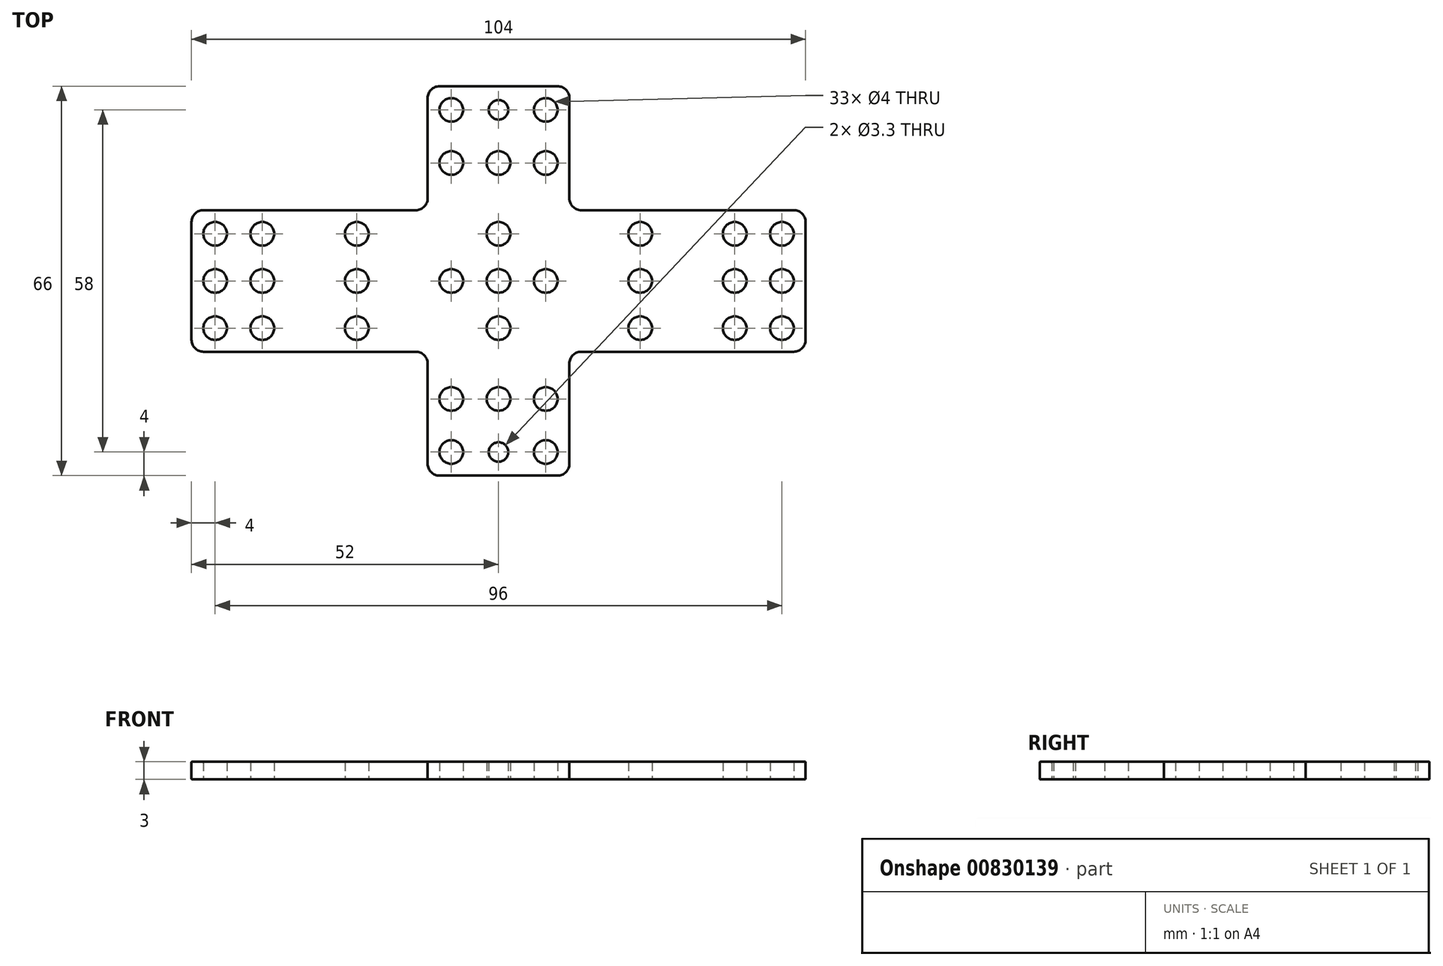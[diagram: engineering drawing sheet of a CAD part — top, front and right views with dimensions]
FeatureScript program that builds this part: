
annotation { "Feature Type Name" : "Feature", "Feature Type Description" : "" }
export const myFeature = defineFeature(function(context is Context, id is Id, definition is map)
    precondition{}
    {
        {
            var Q0;
            Q0=qCreatedBy(makeId("Top.planeOp"),FACE);
            var sketch = newSketch(context, id + "F0", { "sketchPlane" : qUnion([Q0])});
            skLineSegment(sketch, "E0", {"start": v(-10, -33) * mm, "end": v(10, -33) * mm});
            skLineSegment(sketch, "E1", {"start": v(52, -10) * mm, "end": v(52, 10) * mm});
            skLineSegment(sketch, "E2", {"start": v(10, 33) * mm, "end": v(-10, 33) * mm});
            skLineSegment(sketch, "E3", {"start": v(-52, 10) * mm, "end": v(-52, -10) * mm});
            skLineSegment(sketch, "E4", {"start": v(-50, 12) * mm, "end": v(-14, 12) * mm});
            skLineSegment(sketch, "E5", {"start": v(-12, 14) * mm, "end": v(-12, 31) * mm});
            skLineSegment(sketch, "E6", {"start": v(-50, -12) * mm, "end": v(-14, -12) * mm});
            skLineSegment(sketch, "E7", {"start": v(-12, -14) * mm, "end": v(-12, -31) * mm});
            skLineSegment(sketch, "E8", {"start": v(12, 31) * mm, "end": v(12, 14) * mm});
            skLineSegment(sketch, "E9", {"start": v(14, 12) * mm, "end": v(50, 12) * mm});
            skLineSegment(sketch, "E10", {"start": v(50, -12) * mm, "end": v(14, -12) * mm});
            skLineSegment(sketch, "E11", {"start": v(12, -14) * mm, "end": v(12, -31) * mm});
            skPoint(sketch, "E12.visualSharp", {"position": v(-52, 12) * mm});
            skArc(sketch, "E12.filletArc", {"start": v(-50, 12) * mm, "mid": v(-51.41, 11.41) * mm, "end": v(-52, 10) * mm});
            skPoint(sketch, "E13.visualSharp", {"position": v(-12, 12) * mm});
            skArc(sketch, "E13.filletArc", {"start": v(-14, 12) * mm, "mid": v(-12.59, 12.59) * mm, "end": v(-12, 14) * mm});
            skPoint(sketch, "E14.visualSharp", {"position": v(-12, 33) * mm});
            skArc(sketch, "E14.filletArc", {"start": v(-10, 33) * mm, "mid": v(-11.41, 32.41) * mm, "end": v(-12, 31) * mm});
            skPoint(sketch, "E15.visualSharp", {"position": v(12, 33) * mm});
            skArc(sketch, "E15.filletArc", {"start": v(12, 31) * mm, "mid": v(11.41, 32.41) * mm, "end": v(10, 33) * mm});
            skPoint(sketch, "E16.visualSharp", {"position": v(12, 12) * mm});
            skArc(sketch, "E16.filletArc", {"start": v(12, 14) * mm, "mid": v(12.59, 12.59) * mm, "end": v(14, 12) * mm});
            skPoint(sketch, "E17.visualSharp", {"position": v(52, 12) * mm});
            skArc(sketch, "E17.filletArc", {"start": v(52, 10) * mm, "mid": v(51.41, 11.41) * mm, "end": v(50, 12) * mm});
            skPoint(sketch, "E18.visualSharp", {"position": v(52, -12) * mm});
            skArc(sketch, "E18.filletArc", {"start": v(50, -12) * mm, "mid": v(51.41, -11.41) * mm, "end": v(52, -10) * mm});
            skPoint(sketch, "E19.visualSharp", {"position": v(12, -12) * mm});
            skArc(sketch, "E19.filletArc", {"start": v(14, -12) * mm, "mid": v(12.59, -12.59) * mm, "end": v(12, -14) * mm});
            skPoint(sketch, "E20.visualSharp", {"position": v(12, -33) * mm});
            skArc(sketch, "E20.filletArc", {"start": v(10, -33) * mm, "mid": v(11.41, -32.41) * mm, "end": v(12, -31) * mm});
            skPoint(sketch, "E21.visualSharp", {"position": v(-12, -33) * mm});
            skArc(sketch, "E21.filletArc", {"start": v(-12, -31) * mm, "mid": v(-11.41, -32.41) * mm, "end": v(-10, -33) * mm});
            skPoint(sketch, "E22.visualSharp", {"position": v(-12, -12) * mm});
            skArc(sketch, "E22.filletArc", {"start": v(-12, -14) * mm, "mid": v(-12.59, -12.59) * mm, "end": v(-14, -12) * mm});
            skPoint(sketch, "E23.visualSharp", {"position": v(-52, -12) * mm});
            skArc(sketch, "E23.filletArc", {"start": v(-52, -10) * mm, "mid": v(-51.41, -11.41) * mm, "end": v(-50, -12) * mm});
            skPoint(sketch, "E24", {"position": v(0, 0) * mm});
            skPoint(sketch, "E25", {"position": v(8, 0) * mm});
            skPoint(sketch, "E26", {"position": v(0, -8) * mm});
            skPoint(sketch, "E27", {"position": v(-8, 0) * mm});
            skPoint(sketch, "E28", {"position": v(0, 8) * mm});
            skCircle(sketch, "E29", {"center": v(0, 0) * mm, "radius": 2 * mm});
            skCircle(sketch, "E30", {"center": v(8, 0) * mm, "radius": 2 * mm});
            skCircle(sketch, "E31", {"center": v(-8, 0) * mm, "radius": 2 * mm});
            skCircle(sketch, "E32", {"center": v(0, -8) * mm, "radius": 2 * mm});
            skCircle(sketch, "E33", {"center": v(0, 8) * mm, "radius": 2 * mm});
            skCircle(sketch, "E34", {"center": v(24, 0) * mm, "radius": 2 * mm});
            skCircle(sketch, "E35", {"center": v(24, 8) * mm, "radius": 2 * mm});
            skCircle(sketch, "E36", {"center": v(24, -8) * mm, "radius": 2 * mm});
            skCircle(sketch, "E37", {"center": v(40, 0) * mm, "radius": 2 * mm});
            skCircle(sketch, "E38", {"center": v(40, 8) * mm, "radius": 2 * mm});
            skCircle(sketch, "E39", {"center": v(40, -8) * mm, "radius": 2 * mm});
            skCircle(sketch, "E40", {"center": v(48, 0) * mm, "radius": 2 * mm});
            skCircle(sketch, "E41", {"center": v(48, -8) * mm, "radius": 2 * mm});
            skCircle(sketch, "E42", {"center": v(48, 8) * mm, "radius": 2 * mm});
            skCircle(sketch, "E43.MirrorC", {"center": v(-24, -8) * mm, "radius": 2 * mm});
            skCircle(sketch, "E44.MirrorC", {"center": v(-48, 0) * mm, "radius": 2 * mm});
            skCircle(sketch, "E45.MirrorC", {"center": v(-40, 0) * mm, "radius": 2 * mm});
            skCircle(sketch, "E46.MirrorC", {"center": v(-40, 8) * mm, "radius": 2 * mm});
            skCircle(sketch, "E47.MirrorC", {"center": v(-24, 0) * mm, "radius": 2 * mm});
            skCircle(sketch, "E48.MirrorC", {"center": v(-48, 8) * mm, "radius": 2 * mm});
            skCircle(sketch, "E49.MirrorC", {"center": v(-48, -8) * mm, "radius": 2 * mm});
            skCircle(sketch, "E50.MirrorC", {"center": v(-24, 8) * mm, "radius": 2 * mm});
            skCircle(sketch, "E51.MirrorC", {"center": v(-40, -8) * mm, "radius": 2 * mm});
            skCircle(sketch, "E52", {"center": v(0, 20) * mm, "radius": 2 * mm});
            skCircle(sketch, "E53", {"center": v(8, 20) * mm, "radius": 2 * mm});
            skCircle(sketch, "E54", {"center": v(-8, 20) * mm, "radius": 2 * mm});
            skCircle(sketch, "E55.MirrorC", {"center": v(-8, -20) * mm, "radius": 2 * mm});
            skCircle(sketch, "E56.MirrorC", {"center": v(0, -20) * mm, "radius": 2 * mm});
            skCircle(sketch, "E57.MirrorC", {"center": v(8, -20) * mm, "radius": 2 * mm});
            skCircle(sketch, "E58", {"center": v(8, 29) * mm, "radius": 2 * mm});
            skCircle(sketch, "E59", {"center": v(-8, 29) * mm, "radius": 2 * mm});
            skPoint(sketch, "E60", {"position": v(0, 29) * mm});
            skPoint(sketch, "E61.MirrorP", {"position": v(0, -29) * mm});
            skCircle(sketch, "E62.MirrorC", {"center": v(-8, -29) * mm, "radius": 2 * mm});
            skCircle(sketch, "E63.MirrorC", {"center": v(8, -29) * mm, "radius": 2 * mm});
            skSolve(sketch);
        }
        {
            var Q0;
            Q0 = qSketchRegion(id + "F0", true);
            extrude(context, id + "F1", {"entities" : qUnion([Q0]), "depth" : 3 * mm, "offsetDistance" : 25 * mm});
        }
        {
            var Q0;
            Q0=makeQuery(id+"F1.opExtrude","CAP_FACE",FACE,{"disambiguationData":[OSD([sQuery(id+"F0.wireOp",EDGE,"E0"),sQuery(id+"F0.wireOp",EDGE,"E1"),sQuery(id+"F0.wireOp",EDGE,"E2"),sQuery(id+"F0.wireOp",EDGE,"E3"),sQuery(id+"F0.wireOp",EDGE,"E4"),sQuery(id+"F0.wireOp",EDGE,"E5"),sQuery(id+"F0.wireOp",EDGE,"E6"),sQuery(id+"F0.wireOp",EDGE,"E7"),sQuery(id+"F0.wireOp",EDGE,"E8"),sQuery(id+"F0.wireOp",EDGE,"E9"),sQuery(id+"F0.wireOp",EDGE,"E10"),sQuery(id+"F0.wireOp",EDGE,"E11"),sQuery(id+"F0.wireOp",EDGE,"E12.filletArc"),sQuery(id+"F0.wireOp",EDGE,"E13.filletArc"),sQuery(id+"F0.wireOp",EDGE,"E14.filletArc"),sQuery(id+"F0.wireOp",EDGE,"E15.filletArc"),sQuery(id+"F0.wireOp",EDGE,"E16.filletArc"),sQuery(id+"F0.wireOp",EDGE,"E17.filletArc"),sQuery(id+"F0.wireOp",EDGE,"E18.filletArc"),sQuery(id+"F0.wireOp",EDGE,"E19.filletArc"),sQuery(id+"F0.wireOp",EDGE,"E20.filletArc"),sQuery(id+"F0.wireOp",EDGE,"E21.filletArc"),sQuery(id+"F0.wireOp",EDGE,"E22.filletArc"),sQuery(id+"F0.wireOp",EDGE,"E23.filletArc"),sQuery(id+"F0.wireOp",EDGE,"E29"),sQuery(id+"F0.wireOp",EDGE,"E30"),sQuery(id+"F0.wireOp",EDGE,"E31"),sQuery(id+"F0.wireOp",EDGE,"E32"),sQuery(id+"F0.wireOp",EDGE,"E33"),sQuery(id+"F0.wireOp",EDGE,"E34"),sQuery(id+"F0.wireOp",EDGE,"E35"),sQuery(id+"F0.wireOp",EDGE,"E36"),sQuery(id+"F0.wireOp",EDGE,"E37"),sQuery(id+"F0.wireOp",EDGE,"E38"),sQuery(id+"F0.wireOp",EDGE,"E39"),sQuery(id+"F0.wireOp",EDGE,"E40"),sQuery(id+"F0.wireOp",EDGE,"E41"),sQuery(id+"F0.wireOp",EDGE,"E42"),sQuery(id+"F0.wireOp",EDGE,"E43.MirrorC"),sQuery(id+"F0.wireOp",EDGE,"E44.MirrorC"),sQuery(id+"F0.wireOp",EDGE,"E45.MirrorC"),sQuery(id+"F0.wireOp",EDGE,"E46.MirrorC"),sQuery(id+"F0.wireOp",EDGE,"E47.MirrorC"),sQuery(id+"F0.wireOp",EDGE,"E48.MirrorC"),sQuery(id+"F0.wireOp",EDGE,"E49.MirrorC"),sQuery(id+"F0.wireOp",EDGE,"E50.MirrorC"),sQuery(id+"F0.wireOp",EDGE,"E51.MirrorC"),sQuery(id+"F0.wireOp",EDGE,"E52"),sQuery(id+"F0.wireOp",EDGE,"E53"),sQuery(id+"F0.wireOp",EDGE,"E54"),sQuery(id+"F0.wireOp",EDGE,"E58"),sQuery(id+"F0.wireOp",EDGE,"E59"),sQuery(id+"F0.wireOp",EDGE,"E56.MirrorC"),sQuery(id+"F0.wireOp",EDGE,"E55.MirrorC"),sQuery(id+"F0.wireOp",EDGE,"E62.MirrorC"),sQuery(id+"F0.wireOp",EDGE,"E63.MirrorC"),sQuery(id+"F0.wireOp",EDGE,"E57.MirrorC")])],"isStart":true});
            var sketch = newSketch(context, id + "F2", { "sketchPlane" : qUnion([Q0])});
            skPoint(sketch, "E64", {"position": v(0, 29) * mm});
            skPoint(sketch, "E65", {"position": v(0, -29) * mm});
            skSolve(sketch);
        }
        {
            var Q0;
            Q0=sQuery(id+"F2.wireOp",VERTEX,"E64");
            var Q1;
            Q1=sQuery(id+"F2.wireOp",VERTEX,"E65");
            var Q2;
            Q2=makeQuery(id+"F1.opExtrude","SWEPT_BODY",BODY,{"disambiguationData":[OSD([sQuery(id+"F0.wireOp",EDGE,"E0"),sQuery(id+"F0.wireOp",EDGE,"E1"),sQuery(id+"F0.wireOp",EDGE,"E2"),sQuery(id+"F0.wireOp",EDGE,"E3"),sQuery(id+"F0.wireOp",EDGE,"E4"),sQuery(id+"F0.wireOp",EDGE,"E5"),sQuery(id+"F0.wireOp",EDGE,"E6"),sQuery(id+"F0.wireOp",EDGE,"E7"),sQuery(id+"F0.wireOp",EDGE,"E8"),sQuery(id+"F0.wireOp",EDGE,"E9"),sQuery(id+"F0.wireOp",EDGE,"E10"),sQuery(id+"F0.wireOp",EDGE,"E11"),sQuery(id+"F0.wireOp",EDGE,"E12.filletArc"),sQuery(id+"F0.wireOp",EDGE,"E13.filletArc"),sQuery(id+"F0.wireOp",EDGE,"E14.filletArc"),sQuery(id+"F0.wireOp",EDGE,"E15.filletArc"),sQuery(id+"F0.wireOp",EDGE,"E16.filletArc"),sQuery(id+"F0.wireOp",EDGE,"E17.filletArc"),sQuery(id+"F0.wireOp",EDGE,"E18.filletArc"),sQuery(id+"F0.wireOp",EDGE,"E19.filletArc"),sQuery(id+"F0.wireOp",EDGE,"E20.filletArc"),sQuery(id+"F0.wireOp",EDGE,"E21.filletArc"),sQuery(id+"F0.wireOp",EDGE,"E22.filletArc"),sQuery(id+"F0.wireOp",EDGE,"E23.filletArc"),sQuery(id+"F0.wireOp",EDGE,"E29"),sQuery(id+"F0.wireOp",EDGE,"E30"),sQuery(id+"F0.wireOp",EDGE,"E31"),sQuery(id+"F0.wireOp",EDGE,"E32"),sQuery(id+"F0.wireOp",EDGE,"E33"),sQuery(id+"F0.wireOp",EDGE,"E34"),sQuery(id+"F0.wireOp",EDGE,"E35"),sQuery(id+"F0.wireOp",EDGE,"E36"),sQuery(id+"F0.wireOp",EDGE,"E37"),sQuery(id+"F0.wireOp",EDGE,"E38"),sQuery(id+"F0.wireOp",EDGE,"E39"),sQuery(id+"F0.wireOp",EDGE,"E40"),sQuery(id+"F0.wireOp",EDGE,"E41"),sQuery(id+"F0.wireOp",EDGE,"E42"),sQuery(id+"F0.wireOp",EDGE,"E43.MirrorC"),sQuery(id+"F0.wireOp",EDGE,"E44.MirrorC"),sQuery(id+"F0.wireOp",EDGE,"E45.MirrorC"),sQuery(id+"F0.wireOp",EDGE,"E46.MirrorC"),sQuery(id+"F0.wireOp",EDGE,"E47.MirrorC"),sQuery(id+"F0.wireOp",EDGE,"E48.MirrorC"),sQuery(id+"F0.wireOp",EDGE,"E49.MirrorC"),sQuery(id+"F0.wireOp",EDGE,"E50.MirrorC"),sQuery(id+"F0.wireOp",EDGE,"E51.MirrorC"),sQuery(id+"F0.wireOp",EDGE,"E52"),sQuery(id+"F0.wireOp",EDGE,"E53"),sQuery(id+"F0.wireOp",EDGE,"E54"),sQuery(id+"F0.wireOp",EDGE,"E58"),sQuery(id+"F0.wireOp",EDGE,"E59"),sQuery(id+"F0.wireOp",EDGE,"E56.MirrorC"),sQuery(id+"F0.wireOp",EDGE,"E55.MirrorC"),sQuery(id+"F0.wireOp",EDGE,"E62.MirrorC"),sQuery(id+"F0.wireOp",EDGE,"E63.MirrorC"),sQuery(id+"F0.wireOp",EDGE,"E57.MirrorC")])]});
            hole(context, id + "F3", {"style" : HoleStyle.SIMPLE, "endStyle" : HoleEndStyle.THROUGH, "standardTappedOrClearance" : lookupTablePath({ "standard" : "ISO", "engagement" : "75%", "pitch" : "0.7 mm", "size" : "M4", "type" : "Tapped" }), "standardBlindInLast" : lookupTablePath({ "standard" : "ISO", "engagement" : "75%", "pitch" : "0.7 mm", "size" : "M4", "type" : "Tapped" }), "holeDiameter" : 3.3 * mm, "majorDiameter" : 4 * mm, "showTappedDepth" : true, "isTappedThrough" : true, "tappedDepth" : 12 * mm, "tapClearance" : 3, "locations" : qUnion([Q0, Q1]), "scope" : qUnion([Q2])});
        }
        {
            var Q0;
            Q0=makeQuery(id+"F1.opExtrude","CAP_FACE",FACE,{"disambiguationData":[OSD([sQuery(id+"F0.wireOp",EDGE,"E0"),sQuery(id+"F0.wireOp",EDGE,"E1"),sQuery(id+"F0.wireOp",EDGE,"E2"),sQuery(id+"F0.wireOp",EDGE,"E3"),sQuery(id+"F0.wireOp",EDGE,"E4"),sQuery(id+"F0.wireOp",EDGE,"E5"),sQuery(id+"F0.wireOp",EDGE,"E6"),sQuery(id+"F0.wireOp",EDGE,"E7"),sQuery(id+"F0.wireOp",EDGE,"E8"),sQuery(id+"F0.wireOp",EDGE,"E9"),sQuery(id+"F0.wireOp",EDGE,"E10"),sQuery(id+"F0.wireOp",EDGE,"E11"),sQuery(id+"F0.wireOp",EDGE,"E12.filletArc"),sQuery(id+"F0.wireOp",EDGE,"E13.filletArc"),sQuery(id+"F0.wireOp",EDGE,"E14.filletArc"),sQuery(id+"F0.wireOp",EDGE,"E15.filletArc"),sQuery(id+"F0.wireOp",EDGE,"E16.filletArc"),sQuery(id+"F0.wireOp",EDGE,"E17.filletArc"),sQuery(id+"F0.wireOp",EDGE,"E18.filletArc"),sQuery(id+"F0.wireOp",EDGE,"E19.filletArc"),sQuery(id+"F0.wireOp",EDGE,"E20.filletArc"),sQuery(id+"F0.wireOp",EDGE,"E21.filletArc"),sQuery(id+"F0.wireOp",EDGE,"E22.filletArc"),sQuery(id+"F0.wireOp",EDGE,"E23.filletArc"),sQuery(id+"F0.wireOp",EDGE,"E29"),sQuery(id+"F0.wireOp",EDGE,"E30"),sQuery(id+"F0.wireOp",EDGE,"E31"),sQuery(id+"F0.wireOp",EDGE,"E32"),sQuery(id+"F0.wireOp",EDGE,"E33"),sQuery(id+"F0.wireOp",EDGE,"E34"),sQuery(id+"F0.wireOp",EDGE,"E35"),sQuery(id+"F0.wireOp",EDGE,"E36"),sQuery(id+"F0.wireOp",EDGE,"E37"),sQuery(id+"F0.wireOp",EDGE,"E38"),sQuery(id+"F0.wireOp",EDGE,"E39"),sQuery(id+"F0.wireOp",EDGE,"E40"),sQuery(id+"F0.wireOp",EDGE,"E41"),sQuery(id+"F0.wireOp",EDGE,"E42"),sQuery(id+"F0.wireOp",EDGE,"E43.MirrorC"),sQuery(id+"F0.wireOp",EDGE,"E44.MirrorC"),sQuery(id+"F0.wireOp",EDGE,"E45.MirrorC"),sQuery(id+"F0.wireOp",EDGE,"E46.MirrorC"),sQuery(id+"F0.wireOp",EDGE,"E47.MirrorC"),sQuery(id+"F0.wireOp",EDGE,"E48.MirrorC"),sQuery(id+"F0.wireOp",EDGE,"E49.MirrorC"),sQuery(id+"F0.wireOp",EDGE,"E50.MirrorC"),sQuery(id+"F0.wireOp",EDGE,"E51.MirrorC"),sQuery(id+"F0.wireOp",EDGE,"E52"),sQuery(id+"F0.wireOp",EDGE,"E53"),sQuery(id+"F0.wireOp",EDGE,"E54"),sQuery(id+"F0.wireOp",EDGE,"E58"),sQuery(id+"F0.wireOp",EDGE,"E59"),sQuery(id+"F0.wireOp",EDGE,"E56.MirrorC"),sQuery(id+"F0.wireOp",EDGE,"E55.MirrorC"),sQuery(id+"F0.wireOp",EDGE,"E62.MirrorC"),sQuery(id+"F0.wireOp",EDGE,"E63.MirrorC"),sQuery(id+"F0.wireOp",EDGE,"E57.MirrorC")])],"isStart":true});
            var Q1;
            Q1=makeQuery(id+"F1.opExtrude","CAP_FACE",FACE,{"disambiguationData":[OSD([sQuery(id+"F0.wireOp",EDGE,"E0"),sQuery(id+"F0.wireOp",EDGE,"E1"),sQuery(id+"F0.wireOp",EDGE,"E2"),sQuery(id+"F0.wireOp",EDGE,"E3"),sQuery(id+"F0.wireOp",EDGE,"E4"),sQuery(id+"F0.wireOp",EDGE,"E5"),sQuery(id+"F0.wireOp",EDGE,"E6"),sQuery(id+"F0.wireOp",EDGE,"E7"),sQuery(id+"F0.wireOp",EDGE,"E8"),sQuery(id+"F0.wireOp",EDGE,"E9"),sQuery(id+"F0.wireOp",EDGE,"E10"),sQuery(id+"F0.wireOp",EDGE,"E11"),sQuery(id+"F0.wireOp",EDGE,"E12.filletArc"),sQuery(id+"F0.wireOp",EDGE,"E13.filletArc"),sQuery(id+"F0.wireOp",EDGE,"E14.filletArc"),sQuery(id+"F0.wireOp",EDGE,"E15.filletArc"),sQuery(id+"F0.wireOp",EDGE,"E16.filletArc"),sQuery(id+"F0.wireOp",EDGE,"E17.filletArc"),sQuery(id+"F0.wireOp",EDGE,"E18.filletArc"),sQuery(id+"F0.wireOp",EDGE,"E19.filletArc"),sQuery(id+"F0.wireOp",EDGE,"E20.filletArc"),sQuery(id+"F0.wireOp",EDGE,"E21.filletArc"),sQuery(id+"F0.wireOp",EDGE,"E22.filletArc"),sQuery(id+"F0.wireOp",EDGE,"E23.filletArc"),sQuery(id+"F0.wireOp",EDGE,"E29"),sQuery(id+"F0.wireOp",EDGE,"E30"),sQuery(id+"F0.wireOp",EDGE,"E31"),sQuery(id+"F0.wireOp",EDGE,"E32"),sQuery(id+"F0.wireOp",EDGE,"E33"),sQuery(id+"F0.wireOp",EDGE,"E34"),sQuery(id+"F0.wireOp",EDGE,"E35"),sQuery(id+"F0.wireOp",EDGE,"E36"),sQuery(id+"F0.wireOp",EDGE,"E37"),sQuery(id+"F0.wireOp",EDGE,"E38"),sQuery(id+"F0.wireOp",EDGE,"E39"),sQuery(id+"F0.wireOp",EDGE,"E40"),sQuery(id+"F0.wireOp",EDGE,"E41"),sQuery(id+"F0.wireOp",EDGE,"E42"),sQuery(id+"F0.wireOp",EDGE,"E43.MirrorC"),sQuery(id+"F0.wireOp",EDGE,"E44.MirrorC"),sQuery(id+"F0.wireOp",EDGE,"E45.MirrorC"),sQuery(id+"F0.wireOp",EDGE,"E46.MirrorC"),sQuery(id+"F0.wireOp",EDGE,"E47.MirrorC"),sQuery(id+"F0.wireOp",EDGE,"E48.MirrorC"),sQuery(id+"F0.wireOp",EDGE,"E49.MirrorC"),sQuery(id+"F0.wireOp",EDGE,"E50.MirrorC"),sQuery(id+"F0.wireOp",EDGE,"E51.MirrorC"),sQuery(id+"F0.wireOp",EDGE,"E52"),sQuery(id+"F0.wireOp",EDGE,"E53"),sQuery(id+"F0.wireOp",EDGE,"E54"),sQuery(id+"F0.wireOp",EDGE,"E58"),sQuery(id+"F0.wireOp",EDGE,"E59"),sQuery(id+"F0.wireOp",EDGE,"E56.MirrorC"),sQuery(id+"F0.wireOp",EDGE,"E55.MirrorC"),sQuery(id+"F0.wireOp",EDGE,"E62.MirrorC"),sQuery(id+"F0.wireOp",EDGE,"E63.MirrorC"),sQuery(id+"F0.wireOp",EDGE,"E57.MirrorC")])],"isStart":false});
            fillet(context, id + "F4", {"entities" : qUnion([Q0, Q1]), "radius" : 0.1 * mm, "tangentPropagation" : true, "allowEdgeOverflow" : false});
        }
    });
